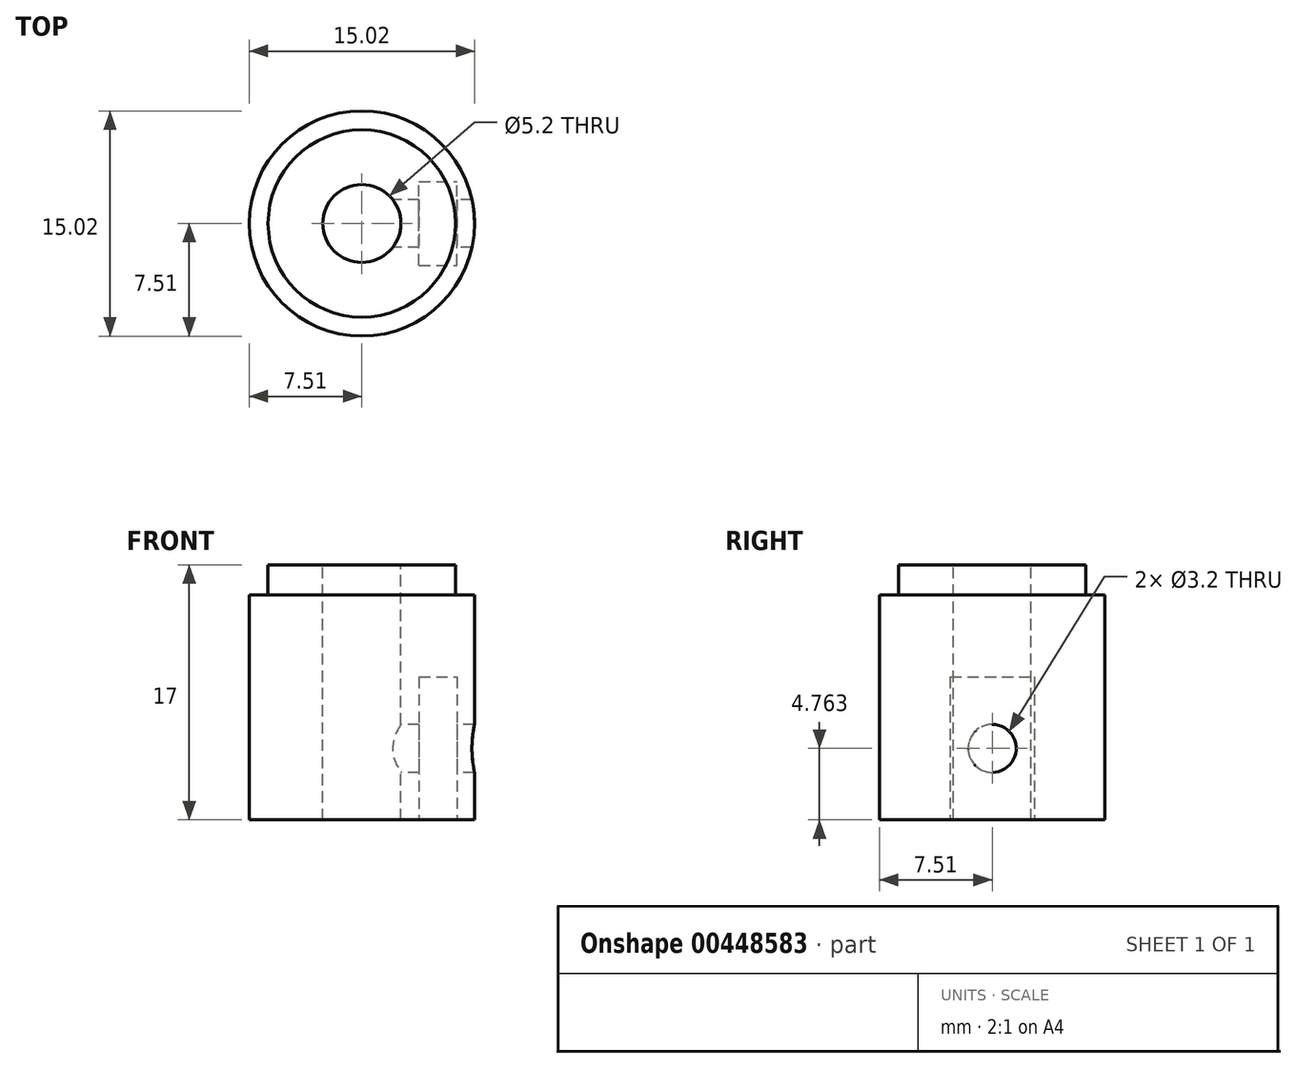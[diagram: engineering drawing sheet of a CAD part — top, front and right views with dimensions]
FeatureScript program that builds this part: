
annotation { "Feature Type Name" : "Feature", "Feature Type Description" : "" }
export const myFeature = defineFeature(function(context is Context, id is Id, definition is map)
    precondition{}
    {
        {
            var Q0;
            Q0=qCreatedBy(makeId("Front.planeOp"),FACE);
            var sketch = newSketch(context, id + "F0", { "sketchPlane" : qUnion([Q0])});
            skLineSegment(sketch, "E0", {"start": v(2.6, 0) * mm, "end": v(2.6, 17) * mm});
            skLineSegment(sketch, "E1", {"start": v(2.6, 17) * mm, "end": v(6.25, 17) * mm});
            skLineSegment(sketch, "E2", {"start": v(6.25, 17) * mm, "end": v(6.25, 15) * mm});
            skLineSegment(sketch, "E3", {"start": v(6.25, 15) * mm, "end": v(7.5, 15) * mm});
            skLineSegment(sketch, "E4", {"start": v(7.5, 15) * mm, "end": v(7.5, 0) * mm});
            skLineSegment(sketch, "E5", {"start": v(7.5, 0) * mm, "end": v(2.6, 0) * mm});
            skLineSegment(sketch, "E6", {"start": v(0, 25.45) * mm, "end": v(0, 0) * mm});
            skSolve(sketch);
        }
        {
            var Q0;
            Q0=makeQuery(id+"F0.imprint","IMPRINT",FACE,{"disambiguationData":[TD([[makeQuery(id+"F0.imprint","IMPRINT",EDGE,{"derivedFrom":sQuery(id+"F0.wireOp",EDGE,"E0")}),-1.0]])]});
            var Q1;
            Q1=sQuery(id+"F0.wireOp",EDGE,"E6");
            revolve(context, id + "F1", {"entities" : qUnion([Q0]), "axis" : qUnion([Q1]), "revolveType" : RevolveType.FULL});
        }
        {
            var Q0;
            Q0=makeQuery(id+"F1.opRevolve","SWEPT_FACE",FACE,{"disambiguationData":[OSD([sQuery(id+"F0.wireOp",EDGE,"E5")])]});
            var sketch = newSketch(context, id + "F2", { "sketchPlane" : qUnion([Q0])});
            skLineSegment(sketch, "E7.bottom", {"start": v(3.81, 2.8) * mm, "end": v(6.35, 2.8) * mm});
            skLineSegment(sketch, "E7.top", {"start": v(3.81, -2.8) * mm, "end": v(6.35, -2.8) * mm});
            skLineSegment(sketch, "E7.left", {"start": v(3.81, 2.8) * mm, "end": v(3.81, -2.8) * mm});
            skLineSegment(sketch, "E7.right", {"start": v(6.35, 2.8) * mm, "end": v(6.35, -2.8) * mm});
            skSolve(sketch);
        }
        {
            var Q0;
            Q0=makeQuery(id+"F2.imprint","IMPRINT",FACE,{"disambiguationData":[TD([[makeQuery(id+"F2.imprint","IMPRINT",EDGE,{"derivedFrom":sQuery(id+"F2.wireOp",EDGE,"E7.bottom")}),-1.0]])]});
            extrude(context, id + "F3", {"entities" : qUnion([Q0]), "operationType" : NewBodyOperationType.REMOVE, "oppositeDirection" : true, "depth" : 9.52 * mm, "offsetDistance" : 25.4 * mm});
        }
        {
            var Q0;
            Q0=qCreatedBy(makeId("Right.planeOp"),FACE);
            var sketch = newSketch(context, id + "F4", { "sketchPlane" : qUnion([Q0])});
            skPoint(sketch, "E8", {"position": v(0, 4.76) * mm});
            skSolve(sketch);
        }
        {
            var Q0;
            Q0=sQuery(id+"F4.wireOp",VERTEX,"E8");
            var Q1;
            Q1=makeQuery(id+"F1.opRevolve","SWEPT_BODY",BODY,{"disambiguationData":[OSD([sQuery(id+"F0.wireOp",EDGE,"E0"),sQuery(id+"F0.wireOp",EDGE,"E1"),sQuery(id+"F0.wireOp",EDGE,"E2"),sQuery(id+"F0.wireOp",EDGE,"E3"),sQuery(id+"F0.wireOp",EDGE,"E4"),sQuery(id+"F0.wireOp",EDGE,"E5")])]});
            hole(context, id + "F5", {"style" : HoleStyle.SIMPLE, "endStyle" : HoleEndStyle.THROUGH, "oppositeDirection" : true, "holeDiameter" : 3.2 * mm, "majorDiameter" : 6.35 * mm, "isTappedThrough" : true, "tappedDepth" : 12.7 * mm, "tapClearance" : 3, "startFromSketch" : true, "locations" : qUnion([Q0]), "scope" : qUnion([Q1])});
        }
    });
